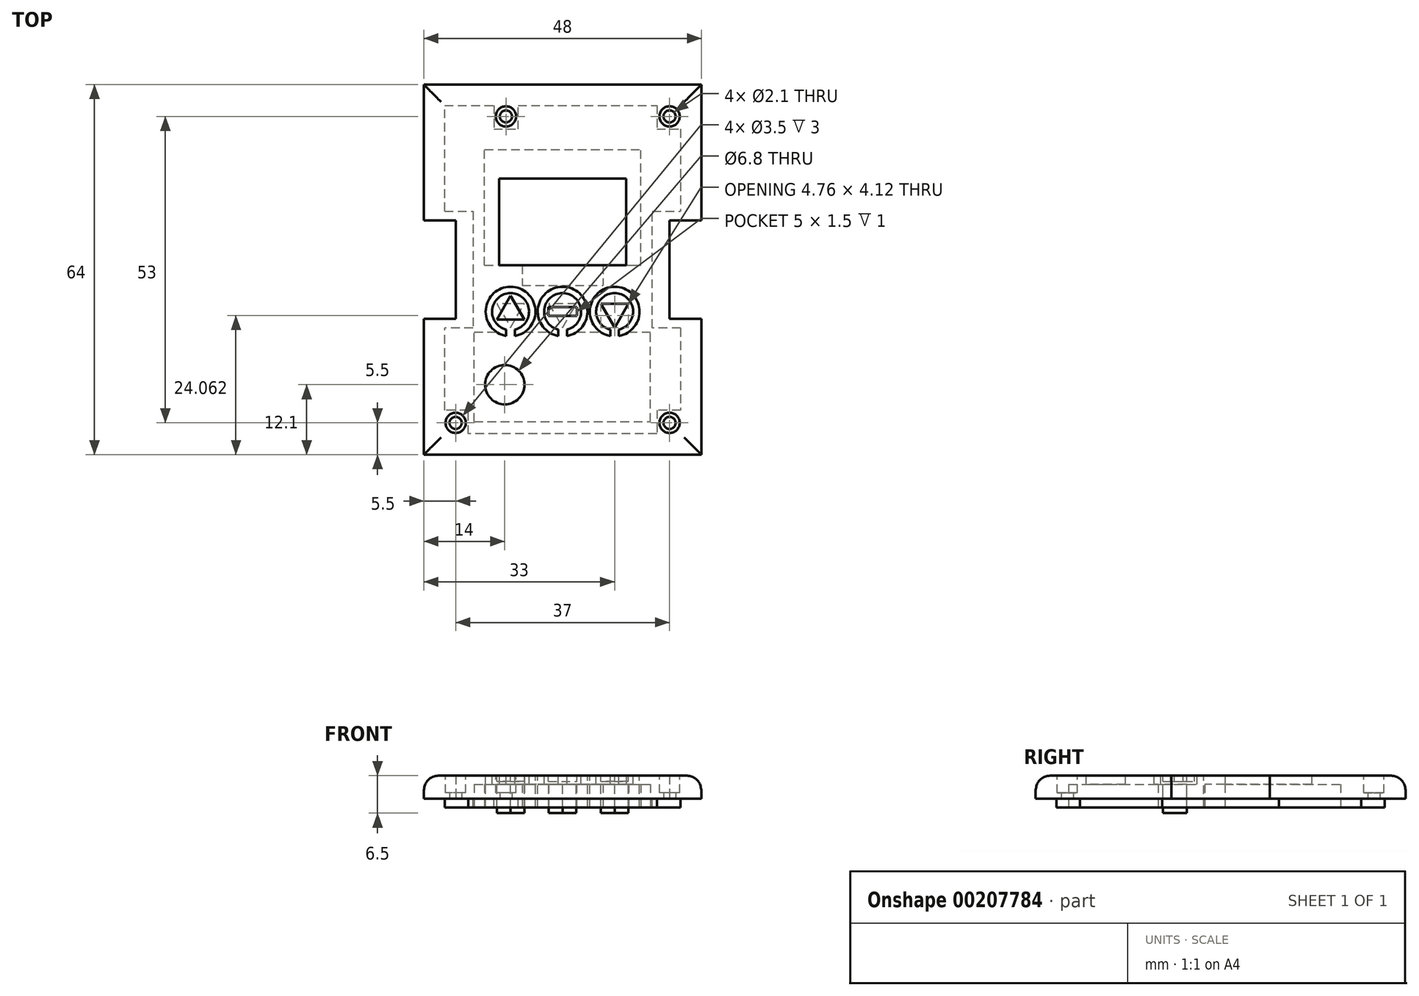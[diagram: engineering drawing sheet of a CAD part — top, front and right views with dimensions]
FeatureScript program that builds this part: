
annotation { "Feature Type Name" : "Feature", "Feature Type Description" : "" }
export const myFeature = defineFeature(function(context is Context, id is Id, definition is map)
    precondition{}
    {
        {
            var Q0;
            Q0=qCreatedBy(makeId("Top.planeOp"),FACE);
            var sketch = newSketch(context, id + "F0", { "sketchPlane" : qUnion([Q0])});
            skLineSegment(sketch, "E0.bottom", {"start": v(-24, 32) * mm, "end": v(24, 32) * mm});
            skLineSegment(sketch, "E0.top", {"start": v(-24, -32) * mm, "end": v(24, -32) * mm});
            skLineSegment(sketch, "E0.left", {"start": v(-24, 32) * mm, "end": v(-24, -32) * mm});
            skLineSegment(sketch, "E0.right", {"start": v(24, 32) * mm, "end": v(24, -32) * mm});
            skSolve(sketch);
        }
        {
            var Q0;
            Q0=makeQuery(id+"F0.imprint","IMPRINT",FACE,{"disambiguationData":[TD([[makeQuery(id+"F0.imprint","IMPRINT",EDGE,{"derivedFrom":sQuery(id+"F0.wireOp",EDGE,"E0.bottom")}),-1.0]])]});
            extrude(context, id + "F1", {"entities" : qUnion([Q0]), "depth" : 4 * mm});
        }
        {
            var Q0;
            Q0=makeQuery(id+"F1.opExtrude","CAP_FACE",FACE,{"disambiguationData":[OSD([sQuery(id+"F0.wireOp",EDGE,"E0.bottom"),sQuery(id+"F0.wireOp",EDGE,"E0.top"),sQuery(id+"F0.wireOp",EDGE,"E0.left"),sQuery(id+"F0.wireOp",EDGE,"E0.right")])],"isStart":true});
            var sketch = newSketch(context, id + "F2", { "sketchPlane" : qUnion([Q0])});
            skLineSegment(sketch, "E1.bottom", {"start": v(-24, 8.5) * mm, "end": v(-18.5, 8.5) * mm});
            skLineSegment(sketch, "E1.top", {"start": v(-24, -8.5) * mm, "end": v(-18.5, -8.5) * mm});
            skLineSegment(sketch, "E1.left", {"start": v(-24, 8.5) * mm, "end": v(-24, -8.5) * mm});
            skLineSegment(sketch, "E1.right", {"start": v(-18.5, 8.5) * mm, "end": v(-18.5, -8.5) * mm});
            skLineSegment(sketch, "E2.bottom", {"start": v(24, 8.5) * mm, "end": v(18.5, 8.5) * mm});
            skLineSegment(sketch, "E2.top", {"start": v(24, -8.5) * mm, "end": v(18.5, -8.5) * mm});
            skLineSegment(sketch, "E2.left", {"start": v(24, 8.5) * mm, "end": v(24, -8.5) * mm});
            skLineSegment(sketch, "E2.right", {"start": v(18.5, 8.5) * mm, "end": v(18.5, -8.5) * mm});
            skSolve(sketch);
        }
        {
            var Q0;
            Q0 = qSketchRegion(id + "F2", true);
            extrude(context, id + "F3", {"entities" : qUnion([Q0]), "operationType" : NewBodyOperationType.REMOVE, "endBound" : BoundingType.UP_TO_NEXT, "oppositeDirection" : true, "depth" : 25 * mm});
        }
        {
            var Q0;
            Q0=makeQuery(id+"F1.opExtrude","CAP_FACE",FACE,{"disambiguationData":[OSD([sQuery(id+"F0.wireOp",EDGE,"E0.bottom"),sQuery(id+"F0.wireOp",EDGE,"E0.top"),sQuery(id+"F0.wireOp",EDGE,"E0.left"),sQuery(id+"F0.wireOp",EDGE,"E0.right")])],"isStart":true});
            var sketch = newSketch(context, id + "F4", { "sketchPlane" : qUnion([Q0])});
            skLineSegment(sketch, "E3", {"start": v(-20.4, -28.4) * mm, "end": v(-11.9, -28.4) * mm});
            skLineSegment(sketch, "E4", {"start": v(-11.9, -28.4) * mm, "end": v(-11.9, -24.3) * mm});
            skLineSegment(sketch, "E5", {"start": v(-11.9, -24.3) * mm, "end": v(-7.7, -24.3) * mm});
            skLineSegment(sketch, "E6", {"start": v(-7.7, -24.3) * mm, "end": v(-7.7, -28.4) * mm});
            skLineSegment(sketch, "E7", {"start": v(20.4, 10.1) * mm, "end": v(20.4, 24.3) * mm});
            skLineSegment(sketch, "E8", {"start": v(20.4, 24.3) * mm, "end": v(16.3, 24.3) * mm});
            skLineSegment(sketch, "E9", {"start": v(16.3, 24.3) * mm, "end": v(16.3, 28.4) * mm});
            skLineSegment(sketch, "E10", {"start": v(16.3, 28.4) * mm, "end": v(-16.3, 28.4) * mm});
            skLineSegment(sketch, "E11", {"start": v(-16.3, 28.4) * mm, "end": v(-16.3, 24.3) * mm});
            skLineSegment(sketch, "E12", {"start": v(-16.3, 24.3) * mm, "end": v(-20.4, 24.3) * mm});
            skLineSegment(sketch, "E13", {"start": v(-20.4, 24.3) * mm, "end": v(-20.4, 10.1) * mm});
            skLineSegment(sketch, "E14", {"start": v(-20.4, -10.1) * mm, "end": v(-20.4, -28.4) * mm});
            skLineSegment(sketch, "E15", {"start": v(16.3, -28.4) * mm, "end": v(16.3, -24.3) * mm});
            skLineSegment(sketch, "E16", {"start": v(16.3, -24.3) * mm, "end": v(20.4, -24.3) * mm});
            skLineSegment(sketch, "E17", {"start": v(-7.7, -28.4) * mm, "end": v(16.3, -28.4) * mm});
            skLineSegment(sketch, "E18", {"start": v(20.4, -24.3) * mm, "end": v(20.4, -10.1) * mm});
            skLineSegment(sketch, "E19", {"start": v(20.4, 10.1) * mm, "end": v(15.5, 10.1) * mm});
            skLineSegment(sketch, "E20", {"start": v(15.5, 10.1) * mm, "end": v(15.5, -10.1) * mm});
            skLineSegment(sketch, "E21", {"start": v(15.5, -10.1) * mm, "end": v(20.4, -10.1) * mm});
            skLineSegment(sketch, "E22", {"start": v(-20.4, -10.1) * mm, "end": v(-15.5, -10.1) * mm});
            skLineSegment(sketch, "E23", {"start": v(-15.5, -10.1) * mm, "end": v(-15.5, 10.1) * mm});
            skLineSegment(sketch, "E24", {"start": v(-15.5, 10.1) * mm, "end": v(-20.4, 10.1) * mm});
            skSolve(sketch);
        }
        {
            var Q0;
            Q0=makeQuery(id+"F4.imprint","IMPRINT",FACE,{"disambiguationData":[TD([[makeQuery(id+"F4.imprint","IMPRINT",EDGE,{"derivedFrom":sQuery(id+"F4.wireOp",EDGE,"E3")}),1.0]])]});
            var Q1;
            Q1=makeQuery(id+"F4.imprint","IMPRINT",FACE,{"disambiguationData":[TD([[makeQuery(id+"F4.imprint","IMPRINT",EDGE,{"derivedFrom":sQuery(id+"F4.wireOp",EDGE,"sVbRoeaL-JvD6-wDni-ZTUx-SvIOOkHwP3DD")}),1.0]])]});
            extrude(context, id + "F5", {"entities" : qUnion([Q0, Q1]), "operationType" : NewBodyOperationType.ADD, "depth" : 1.5 * mm});
        }
        {
            var Q0;
            Q0=makeQuery(id+"F1.opExtrude","CAP_FACE",FACE,{"disambiguationData":[OSD([sQuery(id+"F0.wireOp",EDGE,"E0.bottom"),sQuery(id+"F0.wireOp",EDGE,"E0.top"),sQuery(id+"F0.wireOp",EDGE,"E0.left"),sQuery(id+"F0.wireOp",EDGE,"E0.right")])],"isStart":true});
            var sketch = newSketch(context, id + "F6", { "sketchPlane" : qUnion([Q0])});
            skCircle(sketch, "E25", {"center": v(-9.8, -26.5) * mm, "radius": 1.05 * mm});
            skPoint(sketch, "E25.centerSnap0", {"position": v(-9.8, -24.3) * mm});
            skPoint(sketch, "E25.centerSnap1", {"position": v(-7.7, -26.35) * mm});
            skCircle(sketch, "E26", {"center": v(18.5, -26.5) * mm, "radius": 1.05 * mm});
            skPoint(sketch, "E26.centerSnap0", {"position": v(18.35, -24.3) * mm});
            skPoint(sketch, "E26.centerSnap1", {"position": v(16.3, -26.35) * mm});
            skCircle(sketch, "E27", {"center": v(18.5, 26.5) * mm, "radius": 1.05 * mm});
            skPoint(sketch, "E27.centerSnap0", {"position": v(18.35, 24.3) * mm});
            skPoint(sketch, "E27.centerSnap1", {"position": v(16.3, 26.35) * mm});
            skCircle(sketch, "E28", {"center": v(-18.5, 26.5) * mm, "radius": 1.05 * mm});
            skPoint(sketch, "E28.centerSnap0", {"position": v(-16.3, 26.35) * mm});
            skPoint(sketch, "E28.centerSnap1", {"position": v(-18.35, 24.3) * mm});
            skSolve(sketch);
        }
        {
            var Q0;
            Q0 = qSketchRegion(id + "F6", true);
            extrude(context, id + "F7", {"entities" : qUnion([Q0]), "operationType" : NewBodyOperationType.REMOVE, "endBound" : BoundingType.UP_TO_NEXT, "oppositeDirection" : true, "depth" : 25 * mm});
        }
        {
            var Q0;
            Q0=makeQuery(id+"F5.opExtrude","CAP_FACE",FACE,{"disambiguationData":[OSD([sQuery(id+"F4.wireOp",EDGE,"E3"),sQuery(id+"F4.wireOp",EDGE,"E4"),sQuery(id+"F4.wireOp",EDGE,"E5"),sQuery(id+"F4.wireOp",EDGE,"E6"),sQuery(id+"F4.wireOp",EDGE,"E7"),sQuery(id+"F4.wireOp",EDGE,"E8"),sQuery(id+"F4.wireOp",EDGE,"E9"),sQuery(id+"F4.wireOp",EDGE,"E10"),sQuery(id+"F4.wireOp",EDGE,"E11"),sQuery(id+"F4.wireOp",EDGE,"E12"),sQuery(id+"F4.wireOp",EDGE,"E13"),sQuery(id+"F4.wireOp",EDGE,"E14"),sQuery(id+"F4.wireOp",EDGE,"E15"),sQuery(id+"F4.wireOp",EDGE,"E16"),sQuery(id+"F4.wireOp",EDGE,"E17"),sQuery(id+"F4.wireOp",EDGE,"E18"),sQuery(id+"F4.wireOp",EDGE,"E19"),sQuery(id+"F4.wireOp",EDGE,"E20"),sQuery(id+"F4.wireOp",EDGE,"E21"),sQuery(id+"F4.wireOp",EDGE,"E22"),sQuery(id+"F4.wireOp",EDGE,"E23"),sQuery(id+"F4.wireOp",EDGE,"E24")])],"isStart":false});
            var sketch = newSketch(context, id + "F8", { "sketchPlane" : qUnion([Q0])});
            skLineSegment(sketch, "E29.bottom", {"start": v(-11, -0.75) * mm, "end": v(11, -0.75) * mm});
            skLineSegment(sketch, "E29.top", {"start": v(-11, -15.75) * mm, "end": v(11, -15.75) * mm});
            skLineSegment(sketch, "E29.left", {"start": v(-11, -0.75) * mm, "end": v(-11, -15.75) * mm});
            skLineSegment(sketch, "E29.right", {"start": v(11, -0.75) * mm, "end": v(11, -15.75) * mm});
            skSolve(sketch);
        }
        {
            var Q0;
            Q0 = qSketchRegion(id + "F8", true);
            extrude(context, id + "F9", {"entities" : qUnion([Q0]), "operationType" : NewBodyOperationType.REMOVE, "endBound" : BoundingType.THROUGH_ALL, "oppositeDirection" : true, "depth" : 25 * mm});
        }
        {
            var Q0;
            Q0=makeQuery(id+"F5.opExtrude","CAP_FACE",FACE,{"disambiguationData":[OSD([sQuery(id+"F4.wireOp",EDGE,"E3"),sQuery(id+"F4.wireOp",EDGE,"E4"),sQuery(id+"F4.wireOp",EDGE,"E5"),sQuery(id+"F4.wireOp",EDGE,"E6"),sQuery(id+"F4.wireOp",EDGE,"E7"),sQuery(id+"F4.wireOp",EDGE,"E8"),sQuery(id+"F4.wireOp",EDGE,"E9"),sQuery(id+"F4.wireOp",EDGE,"E10"),sQuery(id+"F4.wireOp",EDGE,"E11"),sQuery(id+"F4.wireOp",EDGE,"E12"),sQuery(id+"F4.wireOp",EDGE,"E13"),sQuery(id+"F4.wireOp",EDGE,"E14"),sQuery(id+"F4.wireOp",EDGE,"E15"),sQuery(id+"F4.wireOp",EDGE,"E16"),sQuery(id+"F4.wireOp",EDGE,"E17"),sQuery(id+"F4.wireOp",EDGE,"E18"),sQuery(id+"F4.wireOp",EDGE,"E19"),sQuery(id+"F4.wireOp",EDGE,"E20"),sQuery(id+"F4.wireOp",EDGE,"E21"),sQuery(id+"F4.wireOp",EDGE,"E22"),sQuery(id+"F4.wireOp",EDGE,"E23"),sQuery(id+"F4.wireOp",EDGE,"E24")])],"isStart":false});
            var sketch = newSketch(context, id + "F10", { "sketchPlane" : qUnion([Q0])});
            skCircle(sketch, "E30", {"center": v(-10, 19.9) * mm, "radius": 3.4 * mm});
            skSolve(sketch);
        }
        {
            var Q0;
            Q0 = qSketchRegion(id + "F10", true);
            extrude(context, id + "F11", {"entities" : qUnion([Q0]), "operationType" : NewBodyOperationType.REMOVE, "endBound" : BoundingType.THROUGH_ALL, "oppositeDirection" : true, "depth" : 25 * mm});
        }
        {
            var Q0;
            Q0=makeQuery(id+"F1.opExtrude","CAP_FACE",FACE,{"disambiguationData":[OSD([sQuery(id+"F0.wireOp",EDGE,"E0.bottom"),sQuery(id+"F0.wireOp",EDGE,"E0.top"),sQuery(id+"F0.wireOp",EDGE,"E0.left"),sQuery(id+"F0.wireOp",EDGE,"E0.right")])],"isStart":false});
            var sketch = newSketch(context, id + "F12", { "sketchPlane" : qUnion([Q0])});
            skArc(sketch, "E31", {"start": v(-0.75, -11.48) * mm, "mid": v(0, -2.95) * mm, "end": v(0.75, -11.48) * mm});
            skArc(sketch, "E32", {"start": v(-0.75, -10.36) * mm, "mid": v(0, -4.05) * mm, "end": v(0.75, -10.36) * mm});
            skLineSegment(sketch, "E33", {"start": v(-0.75, -11.48) * mm, "end": v(-0.75, -10.36) * mm});
            skLineSegment(sketch, "E34", {"start": v(0.75, -11.48) * mm, "end": v(0.75, -10.36) * mm});
            skArc(sketch, "E35", {"start": v(8.25, -11.48) * mm, "mid": v(9, -2.95) * mm, "end": v(9.75, -11.48) * mm});
            skArc(sketch, "E36", {"start": v(8.25, -10.36) * mm, "mid": v(9, -4.05) * mm, "end": v(9.75, -10.36) * mm});
            skLineSegment(sketch, "E37", {"start": v(8.25, -11.48) * mm, "end": v(8.25, -10.36) * mm});
            skLineSegment(sketch, "E38", {"start": v(9.75, -11.48) * mm, "end": v(9.75, -10.36) * mm});
            skArc(sketch, "E39", {"start": v(-9.75, -11.48) * mm, "mid": v(-9, -2.95) * mm, "end": v(-8.25, -11.48) * mm});
            skArc(sketch, "E40", {"start": v(-9.75, -10.36) * mm, "mid": v(-9, -4.05) * mm, "end": v(-8.25, -10.36) * mm});
            skLineSegment(sketch, "E41", {"start": v(-9.75, -11.48) * mm, "end": v(-9.75, -10.36) * mm});
            skLineSegment(sketch, "E42", {"start": v(-8.25, -11.48) * mm, "end": v(-8.25, -10.36) * mm});
            skSolve(sketch);
        }
        {
            var Q0;
            Q0 = qSketchRegion(id + "F12", true);
            extrude(context, id + "F13", {"entities" : qUnion([Q0]), "operationType" : NewBodyOperationType.REMOVE, "endBound" : BoundingType.THROUGH_ALL, "oppositeDirection" : true, "depth" : 25 * mm});
        }
        {
            var Q0;
            Q0=makeQuery(id+"F5.opExtrude","CAP_FACE",FACE,{"disambiguationData":[OSD([sQuery(id+"F4.wireOp",EDGE,"E3"),sQuery(id+"F4.wireOp",EDGE,"E4"),sQuery(id+"F4.wireOp",EDGE,"E5"),sQuery(id+"F4.wireOp",EDGE,"E6"),sQuery(id+"F4.wireOp",EDGE,"E7"),sQuery(id+"F4.wireOp",EDGE,"E8"),sQuery(id+"F4.wireOp",EDGE,"E9"),sQuery(id+"F4.wireOp",EDGE,"E10"),sQuery(id+"F4.wireOp",EDGE,"E11"),sQuery(id+"F4.wireOp",EDGE,"E12"),sQuery(id+"F4.wireOp",EDGE,"E13"),sQuery(id+"F4.wireOp",EDGE,"E14"),sQuery(id+"F4.wireOp",EDGE,"E15"),sQuery(id+"F4.wireOp",EDGE,"E16"),sQuery(id+"F4.wireOp",EDGE,"E17"),sQuery(id+"F4.wireOp",EDGE,"E18"),sQuery(id+"F4.wireOp",EDGE,"E19"),sQuery(id+"F4.wireOp",EDGE,"E20"),sQuery(id+"F4.wireOp",EDGE,"E21"),sQuery(id+"F4.wireOp",EDGE,"E22"),sQuery(id+"F4.wireOp",EDGE,"E23"),sQuery(id+"F4.wireOp",EDGE,"E24")])],"isStart":false});
            var sketch = newSketch(context, id + "F14", { "sketchPlane" : qUnion([Q0])});
            skLineSegment(sketch, "E43.bottom", {"start": v(-13.5, -0.75) * mm, "end": v(13.5, -0.75) * mm});
            skLineSegment(sketch, "E43.top", {"start": v(-13.5, -20.75) * mm, "end": v(13.5, -20.75) * mm});
            skLineSegment(sketch, "E43.left", {"start": v(-13.5, -0.75) * mm, "end": v(-13.5, -20.75) * mm});
            skLineSegment(sketch, "E43.right", {"start": v(13.5, -0.75) * mm, "end": v(13.5, -20.75) * mm});
            skLineSegment(sketch, "E44.bottom", {"start": v(-7, -0.75) * mm, "end": v(7, -0.75) * mm});
            skLineSegment(sketch, "E44.top", {"start": v(-7, 2.75) * mm, "end": v(7, 2.75) * mm});
            skLineSegment(sketch, "E44.left", {"start": v(-7, -0.75) * mm, "end": v(-7, 2.75) * mm});
            skLineSegment(sketch, "E44.right", {"start": v(7, -0.75) * mm, "end": v(7, 2.75) * mm});
            skSolve(sketch);
        }
        {
            var Q0;
            Q0 = qSketchRegion(id + "F14", true);
            extrude(context, id + "F15", {"entities" : qUnion([Q0]), "operationType" : NewBodyOperationType.REMOVE, "oppositeDirection" : true, "depth" : 4 * mm});
        }
        {
            var Q0;
            Q0=makeQuery(id+"F1.opExtrude","CAP_FACE",FACE,{"disambiguationData":[OSD([sQuery(id+"F0.wireOp",EDGE,"E0.bottom"),sQuery(id+"F0.wireOp",EDGE,"E0.top"),sQuery(id+"F0.wireOp",EDGE,"E0.left"),sQuery(id+"F0.wireOp",EDGE,"E0.right")])],"isStart":false});
            var sketch = newSketch(context, id + "F16", { "sketchPlane" : qUnion([Q0])});
            skCircle(sketch, "E45.cCircle", {"center": v(9, -7.25) * mm, "radius": 2.75 * mm, "construction": true});
            skLineSegment(sketch, "E45.0", {"start": v(6.62, -5.87) * mm, "end": v(11.38, -5.87) * mm});
            skLineSegment(sketch, "E45.1", {"start": v(11.38, -5.87) * mm, "end": v(9, -10) * mm});
            skLineSegment(sketch, "E45.2", {"start": v(9, -10) * mm, "end": v(6.62, -5.87) * mm});
            skCircle(sketch, "E46.cCircle", {"center": v(-9, -7.25) * mm, "radius": 2.75 * mm, "construction": true});
            skLineSegment(sketch, "E46.0", {"start": v(-11.38, -8.62) * mm, "end": v(-9, -4.5) * mm});
            skLineSegment(sketch, "E46.1", {"start": v(-9, -4.5) * mm, "end": v(-6.62, -8.62) * mm});
            skLineSegment(sketch, "E46.2", {"start": v(-6.62, -8.62) * mm, "end": v(-11.38, -8.62) * mm});
            skLineSegment(sketch, "E47.bottom", {"start": v(-2.5, -8) * mm, "end": v(2.5, -8) * mm});
            skLineSegment(sketch, "E47.top", {"start": v(-2.5, -6.5) * mm, "end": v(2.5, -6.5) * mm});
            skLineSegment(sketch, "E47.left", {"start": v(-2.5, -8) * mm, "end": v(-2.5, -6.5) * mm});
            skLineSegment(sketch, "E47.right", {"start": v(2.5, -8) * mm, "end": v(2.5, -6.5) * mm});
            skPoint(sketch, "E47.middle", {"position": v(0, -7.25) * mm});
            skSolve(sketch);
        }
        {
            var Q0;
            Q0 = qSketchRegion(id + "F16", true);
            extrude(context, id + "F17", {"entities" : qUnion([Q0]), "operationType" : NewBodyOperationType.REMOVE, "oppositeDirection" : true, "depth" : 1 * mm});
        }
        {
            var Q0;
            Q0=makeQuery(id+"F5.opExtrude","CAP_FACE",FACE,{"disambiguationData":[OSD([sQuery(id+"F4.wireOp",EDGE,"E3"),sQuery(id+"F4.wireOp",EDGE,"E4"),sQuery(id+"F4.wireOp",EDGE,"E5"),sQuery(id+"F4.wireOp",EDGE,"E6"),sQuery(id+"F4.wireOp",EDGE,"E7"),sQuery(id+"F4.wireOp",EDGE,"E8"),sQuery(id+"F4.wireOp",EDGE,"E9"),sQuery(id+"F4.wireOp",EDGE,"E10"),sQuery(id+"F4.wireOp",EDGE,"E11"),sQuery(id+"F4.wireOp",EDGE,"E12"),sQuery(id+"F4.wireOp",EDGE,"E13"),sQuery(id+"F4.wireOp",EDGE,"E14"),sQuery(id+"F4.wireOp",EDGE,"E15"),sQuery(id+"F4.wireOp",EDGE,"E16"),sQuery(id+"F4.wireOp",EDGE,"E17"),sQuery(id+"F4.wireOp",EDGE,"E18"),sQuery(id+"F4.wireOp",EDGE,"E19"),sQuery(id+"F4.wireOp",EDGE,"E20"),sQuery(id+"F4.wireOp",EDGE,"E21"),sQuery(id+"F4.wireOp",EDGE,"E22"),sQuery(id+"F4.wireOp",EDGE,"E23"),sQuery(id+"F4.wireOp",EDGE,"E24")])],"isStart":false});
            var sketch = newSketch(context, id + "F18", { "sketchPlane" : qUnion([Q0])});
            skCircle(sketch, "E48", {"center": v(-9, 7.25) * mm, "radius": 4.3 * mm});
            skCircle(sketch, "E49", {"center": v(0, 7.25) * mm, "radius": 4.3 * mm});
            skCircle(sketch, "E50", {"center": v(9, 7.25) * mm, "radius": 4.3 * mm});
            skLineSegment(sketch, "E51.bottom", {"start": v(-15.3, 26.3) * mm, "end": v(15.2, 26.3) * mm});
            skLineSegment(sketch, "E51.top", {"start": v(-15.3, 10.8) * mm, "end": v(15.2, 10.8) * mm});
            skLineSegment(sketch, "E51.left", {"start": v(-15.3, 26.3) * mm, "end": v(-15.3, 10.8) * mm});
            skLineSegment(sketch, "E51.right", {"start": v(15.2, 26.3) * mm, "end": v(15.2, 10.8) * mm});
            skSolve(sketch);
        }
        {
            var Q0;
            Q0 = qSketchRegion(id + "F18", true);
            extrude(context, id + "F19", {"entities" : qUnion([Q0]), "operationType" : NewBodyOperationType.REMOVE, "oppositeDirection" : true, "depth" : 4 * mm});
        }
        {
            var Q0;
            Q0=makeQuery(id+"F19.boolean.opBoolean","COPY",FACE,{"derivedFrom":makeQuery(id+"F19.opExtrude","CAP_FACE",FACE,{"disambiguationData":[OSD([sQuery(id+"F18.wireOp",EDGE,"E50")])],"isStart":false})});
            var sketch = newSketch(context, id + "F20", { "sketchPlane" : qUnion([Q0])});
            skCircle(sketch, "E52.cCircle", {"center": v(9, 7.25) * mm, "radius": 2.75 * mm, "construction": true});
            skLineSegment(sketch, "E52.0", {"start": v(11.38, 5.87) * mm, "end": v(6.62, 5.87) * mm});
            skLineSegment(sketch, "E52.1", {"start": v(6.62, 5.87) * mm, "end": v(9, 10) * mm});
            skLineSegment(sketch, "E52.2", {"start": v(9, 10) * mm, "end": v(11.38, 5.87) * mm});
            skCircle(sketch, "E53.cCircle", {"center": v(0, 7.25) * mm, "radius": 2.75 * mm, "construction": true});
            skLineSegment(sketch, "E53.0", {"start": v(2.38, 5.87) * mm, "end": v(-2.38, 5.87) * mm});
            skLineSegment(sketch, "E53.1", {"start": v(-2.38, 5.87) * mm, "end": v(0, 10) * mm});
            skLineSegment(sketch, "E53.2", {"start": v(0, 10) * mm, "end": v(2.38, 5.87) * mm});
            skCircle(sketch, "E54.cCircle", {"center": v(-9, 7.25) * mm, "radius": 2.75 * mm, "construction": true});
            skLineSegment(sketch, "E54.0", {"start": v(-6.62, 5.87) * mm, "end": v(-11.38, 5.87) * mm});
            skLineSegment(sketch, "E54.1", {"start": v(-11.38, 5.87) * mm, "end": v(-9, 10) * mm});
            skLineSegment(sketch, "E54.2", {"start": v(-9, 10) * mm, "end": v(-6.62, 5.87) * mm});
            skSolve(sketch);
        }
        {
            var Q0;
            Q0 = qSketchRegion(id + "F20", true);
            extrude(context, id + "F21", {"entities" : qUnion([Q0]), "operationType" : NewBodyOperationType.ADD, "depth" : 5 * mm});
        }
        {
            var Q0;
            Q0=makeQuery(id+"F1.opExtrude","CAP_EDGE",EDGE,{"disambiguationData":[OSD([sQuery(id+"F0.wireOp",EDGE,"E0.top")])],"isStart":false});
            var Q1;
            {var subQ0=sQuery(id+"F0.wireOp",EDGE,"E0.right");var subQ1=sQuery(id+"F0.wireOp",EDGE,"E0.top");Q1=makeQuery(id+"F3.boolean.opBoolean","SPLIT",EDGE,{"disambiguationData":[TD([makeQuery(id+"F1.opExtrude","SWEPT_FACE",FACE,{"disambiguationData":[OSD([subQ1])]})])],"derivedFrom":makeQuery(id+"F1.opExtrude","CAP_EDGE",EDGE,{"disambiguationData":[OSD([subQ0])],"isStart":false})});}
            var Q2;
            Q2=makeQuery(id+"F3.boolean.opBoolean","COPY",EDGE,{"derivedFrom":makeQuery(id+"F3.opExtrude","TWEAK_EDGE",EDGE,{"derivedFrom":[makeQuery(id+"F1.opExtrude","CAP_FACE",FACE,{"disambiguationData":[OSD([sQuery(id+"F0.wireOp",EDGE,"E0.bottom"),sQuery(id+"F0.wireOp",EDGE,"E0.top"),sQuery(id+"F0.wireOp",EDGE,"E0.left"),sQuery(id+"F0.wireOp",EDGE,"E0.right")])],"isStart":false}),makeQuery(id+"F2.imprint","IMPRINT",EDGE,{"derivedFrom":sQuery(id+"F2.wireOp",EDGE,"E2.bottom")})]})});
            var Q3;
            Q3=makeQuery(id+"F3.boolean.opBoolean","COPY",EDGE,{"derivedFrom":makeQuery(id+"F3.opExtrude","TWEAK_EDGE",EDGE,{"derivedFrom":[makeQuery(id+"F1.opExtrude","CAP_FACE",FACE,{"disambiguationData":[OSD([sQuery(id+"F0.wireOp",EDGE,"E0.bottom"),sQuery(id+"F0.wireOp",EDGE,"E0.top"),sQuery(id+"F0.wireOp",EDGE,"E0.left"),sQuery(id+"F0.wireOp",EDGE,"E0.right")])],"isStart":false}),makeQuery(id+"F2.imprint","IMPRINT",EDGE,{"derivedFrom":sQuery(id+"F2.wireOp",EDGE,"E2.right")})]})});
            var Q4;
            Q4=makeQuery(id+"F3.boolean.opBoolean","COPY",EDGE,{"derivedFrom":makeQuery(id+"F3.opExtrude","TWEAK_EDGE",EDGE,{"derivedFrom":[makeQuery(id+"F1.opExtrude","CAP_FACE",FACE,{"disambiguationData":[OSD([sQuery(id+"F0.wireOp",EDGE,"E0.bottom"),sQuery(id+"F0.wireOp",EDGE,"E0.top"),sQuery(id+"F0.wireOp",EDGE,"E0.left"),sQuery(id+"F0.wireOp",EDGE,"E0.right")])],"isStart":false}),makeQuery(id+"F2.imprint","IMPRINT",EDGE,{"derivedFrom":sQuery(id+"F2.wireOp",EDGE,"E2.top")})]})});
            var Q5;
            {var subQ0=sQuery(id+"F0.wireOp",EDGE,"E0.bottom");var subQ1=sQuery(id+"F0.wireOp",EDGE,"E0.right");Q5=makeQuery(id+"F3.boolean.opBoolean","SPLIT",EDGE,{"disambiguationData":[TD([makeQuery(id+"F1.opExtrude","SWEPT_FACE",FACE,{"disambiguationData":[OSD([subQ0])]})])],"derivedFrom":makeQuery(id+"F1.opExtrude","CAP_EDGE",EDGE,{"disambiguationData":[OSD([subQ1])],"isStart":false})});}
            var Q6;
            Q6=makeQuery(id+"F1.opExtrude","CAP_EDGE",EDGE,{"disambiguationData":[OSD([sQuery(id+"F0.wireOp",EDGE,"E0.bottom")])],"isStart":false});
            var Q7;
            {var subQ0=sQuery(id+"F0.wireOp",EDGE,"E0.bottom");var subQ1=sQuery(id+"F0.wireOp",EDGE,"E0.left");Q7=makeQuery(id+"F3.boolean.opBoolean","SPLIT",EDGE,{"disambiguationData":[TD([makeQuery(id+"F1.opExtrude","SWEPT_FACE",FACE,{"disambiguationData":[OSD([subQ0])]})])],"derivedFrom":makeQuery(id+"F1.opExtrude","CAP_EDGE",EDGE,{"disambiguationData":[OSD([subQ1])],"isStart":false})});}
            var Q8;
            Q8=makeQuery(id+"F3.boolean.opBoolean","COPY",EDGE,{"derivedFrom":makeQuery(id+"F3.opExtrude","TWEAK_EDGE",EDGE,{"derivedFrom":[makeQuery(id+"F1.opExtrude","CAP_FACE",FACE,{"disambiguationData":[OSD([sQuery(id+"F0.wireOp",EDGE,"E0.bottom"),sQuery(id+"F0.wireOp",EDGE,"E0.top"),sQuery(id+"F0.wireOp",EDGE,"E0.left"),sQuery(id+"F0.wireOp",EDGE,"E0.right")])],"isStart":false}),makeQuery(id+"F2.imprint","IMPRINT",EDGE,{"derivedFrom":sQuery(id+"F2.wireOp",EDGE,"E1.top")})]})});
            var Q9;
            Q9=makeQuery(id+"F3.boolean.opBoolean","COPY",EDGE,{"derivedFrom":makeQuery(id+"F3.opExtrude","TWEAK_EDGE",EDGE,{"derivedFrom":[makeQuery(id+"F1.opExtrude","CAP_FACE",FACE,{"disambiguationData":[OSD([sQuery(id+"F0.wireOp",EDGE,"E0.bottom"),sQuery(id+"F0.wireOp",EDGE,"E0.top"),sQuery(id+"F0.wireOp",EDGE,"E0.left"),sQuery(id+"F0.wireOp",EDGE,"E0.right")])],"isStart":false}),makeQuery(id+"F2.imprint","IMPRINT",EDGE,{"derivedFrom":sQuery(id+"F2.wireOp",EDGE,"E1.right")})]})});
            var Q10;
            Q10=makeQuery(id+"F3.boolean.opBoolean","COPY",EDGE,{"derivedFrom":makeQuery(id+"F3.opExtrude","TWEAK_EDGE",EDGE,{"derivedFrom":[makeQuery(id+"F1.opExtrude","CAP_FACE",FACE,{"disambiguationData":[OSD([sQuery(id+"F0.wireOp",EDGE,"E0.bottom"),sQuery(id+"F0.wireOp",EDGE,"E0.top"),sQuery(id+"F0.wireOp",EDGE,"E0.left"),sQuery(id+"F0.wireOp",EDGE,"E0.right")])],"isStart":false}),makeQuery(id+"F2.imprint","IMPRINT",EDGE,{"derivedFrom":sQuery(id+"F2.wireOp",EDGE,"E1.bottom")})]})});
            var Q11;
            {var subQ0=sQuery(id+"F0.wireOp",EDGE,"E0.left");var subQ1=sQuery(id+"F0.wireOp",EDGE,"E0.top");Q11=makeQuery(id+"F3.boolean.opBoolean","SPLIT",EDGE,{"disambiguationData":[TD([makeQuery(id+"F1.opExtrude","SWEPT_FACE",FACE,{"disambiguationData":[OSD([subQ1])]})])],"derivedFrom":makeQuery(id+"F1.opExtrude","CAP_EDGE",EDGE,{"disambiguationData":[OSD([subQ0])],"isStart":false})});}
            fillet(context, id + "F22", {"entities" : qUnion([Q0, Q1, Q2, Q3, Q4, Q5, Q6, Q7, Q8, Q9, Q10, Q11]), "radius" : 3 * mm, "tangentPropagation" : true, "rho" : 0.5, "crossSection" : FilletCrossSection.CONIC, "allowEdgeOverflow" : false});
        }
        {
            var Q0;
            Q0=makeQuery(id+"F1.opExtrude","CAP_FACE",FACE,{"disambiguationData":[OSD([sQuery(id+"F0.wireOp",EDGE,"E0.bottom"),sQuery(id+"F0.wireOp",EDGE,"E0.top"),sQuery(id+"F0.wireOp",EDGE,"E0.left"),sQuery(id+"F0.wireOp",EDGE,"E0.right")])],"isStart":false});
            var sketch = newSketch(context, id + "F23", { "sketchPlane" : qUnion([Q0])});
            skCircle(sketch, "E55", {"center": v(-9.8, 26.5) * mm, "radius": 1.75 * mm});
            skCircle(sketch, "E56", {"center": v(18.5, 26.5) * mm, "radius": 1.75 * mm});
            skCircle(sketch, "E57", {"center": v(-18.5, -26.5) * mm, "radius": 1.75 * mm});
            skCircle(sketch, "E58", {"center": v(18.5, -26.5) * mm, "radius": 1.75 * mm});
            skSolve(sketch);
        }
        {
            var Q0;
            Q0 = qSketchRegion(id + "F23", true);
            extrude(context, id + "F24", {"entities" : qUnion([Q0]), "operationType" : NewBodyOperationType.REMOVE, "oppositeDirection" : true, "depth" : 3 * mm});
        }
    });
